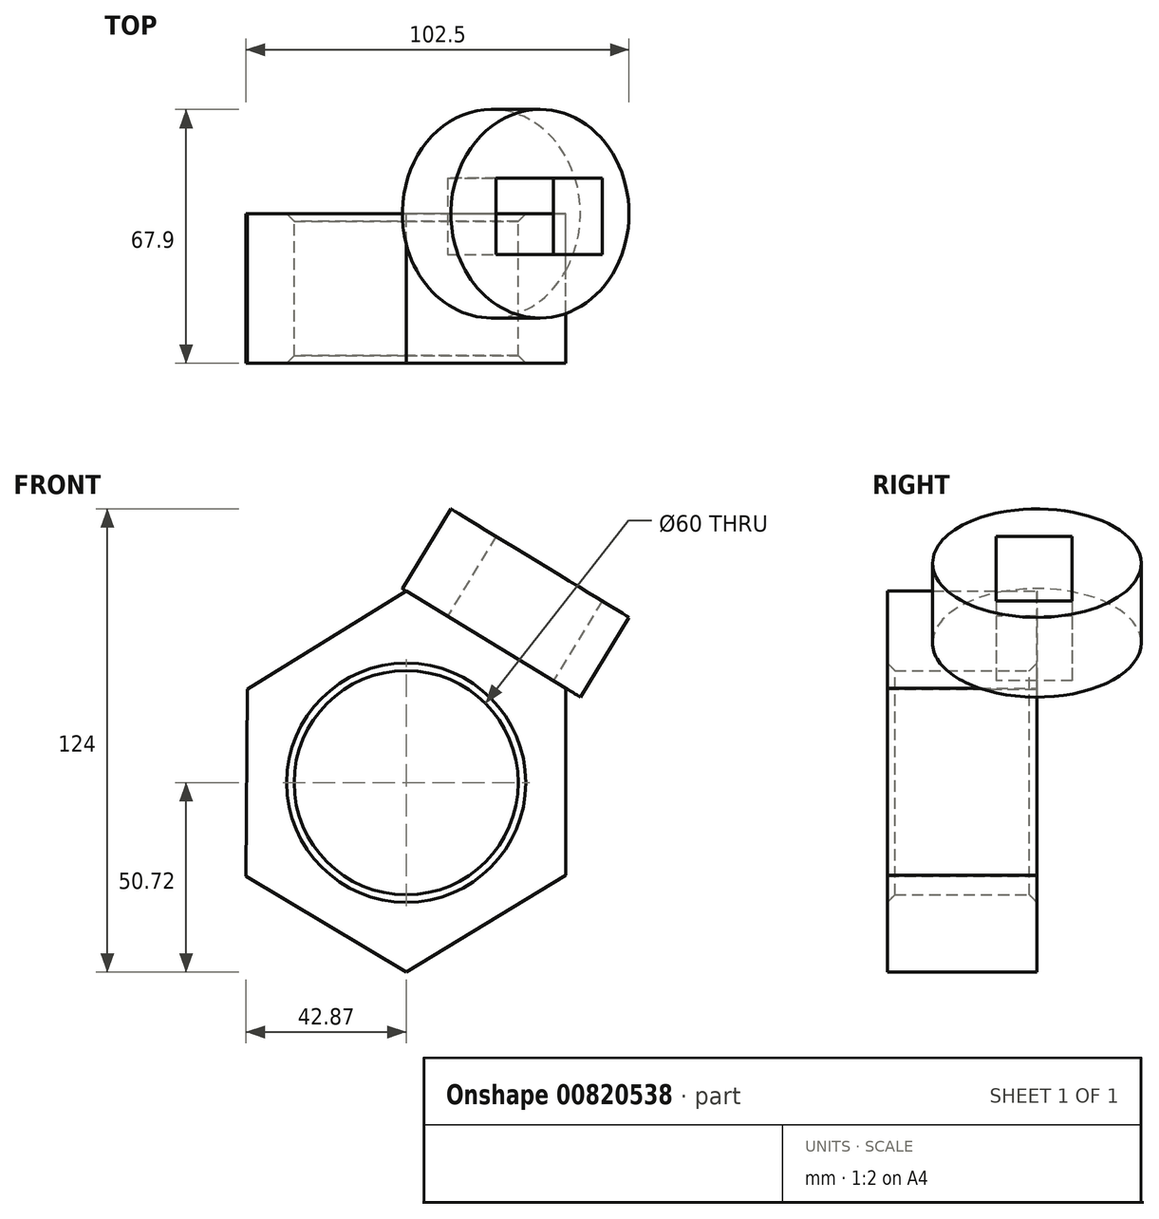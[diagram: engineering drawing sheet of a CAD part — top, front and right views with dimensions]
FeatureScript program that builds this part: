
annotation { "Feature Type Name" : "Feature", "Feature Type Description" : "" }
export const myFeature = defineFeature(function(context is Context, id is Id, definition is map)
    precondition{}
    {
        {
            var Q0;
            Q0=qCreatedBy(makeId("Front.planeOp"),FACE);
            var sketch = newSketch(context, id + "F0", { "sketchPlane" : qUnion([Q0])});
            skCircle(sketch, "E0", {"center": v(0, 0) * mm, "radius": 30 * mm});
            skLineSegment(sketch, "E1", {"start": v(-42.52, 25) * mm, "end": v(0, 51.3) * mm});
            skLineSegment(sketch, "E2", {"start": v(0, 51.3) * mm, "end": v(42.7, 25.29) * mm});
            skLineSegment(sketch, "E3", {"start": v(42.7, 25.29) * mm, "end": v(42.7, -24.71) * mm});
            skLineSegment(sketch, "E4", {"start": v(42.7, -24.71) * mm, "end": v(0, -50.72) * mm});
            skLineSegment(sketch, "E5", {"start": v(0, -50.72) * mm, "end": v(-42.87, -25) * mm});
            skLineSegment(sketch, "E6", {"start": v(-42.52, 25) * mm, "end": v(-42.87, -25) * mm});
            skSolve(sketch);
        }
        {
            var Q0;
            Q0=makeQuery(id+"F0.imprint","IMPRINT",FACE,{"disambiguationData":[TD([[makeQuery(id+"F0.imprint","IMPRINT",EDGE,{"derivedFrom":sQuery(id+"F0.wireOp",EDGE,"E0")}),-1.0]])]});
            extrude(context, id + "F1", {"entities" : qUnion([Q0]), "depth" : 40 * mm, "offsetDistance" : 25 * mm});
        }
        {
            var Q0;
            Q0=makeQuery(id+"F1.opExtrude","CAP_EDGE",EDGE,{"disambiguationData":[OSD([sQuery(id+"F0.wireOp",EDGE,"E0")])],"isStart":false});
            var Q1;
            Q1=makeQuery(id+"F1.opExtrude","CAP_EDGE",EDGE,{"disambiguationData":[OSD([sQuery(id+"F0.wireOp",EDGE,"E0")])],"isStart":true});
            chamfer(context, id + "F2", {"entities" : qUnion([Q0, Q1]), "width" : 2 * mm, "tangentPropagation" : true});
        }
        {
            var Q0;
            Q0=makeQuery(id+"F1.opExtrude","SWEPT_FACE",FACE,{"disambiguationData":[OSD([sQuery(id+"F0.wireOp",EDGE,"E2")])]});
            var sketch = newSketch(context, id + "F3", { "sketchPlane" : qUnion([Q0])});
            skCircle(sketch, "E7", {"center": v(0, 0) * mm, "radius": 27.9 * mm});
            skLineSegment(sketch, "E8.bottom", {"start": v(-13.76, 9.48) * mm, "end": v(19.48, 9.48) * mm});
            skLineSegment(sketch, "E8.top", {"start": v(-13.76, -10.9) * mm, "end": v(19.48, -10.9) * mm});
            skLineSegment(sketch, "E8.left", {"start": v(-13.76, 9.48) * mm, "end": v(-13.76, -10.9) * mm});
            skLineSegment(sketch, "E8.right", {"start": v(19.48, 9.48) * mm, "end": v(19.48, -10.9) * mm});
            skSolve(sketch);
        }
        {
            var Q0;
            Q0 = qSketchRegion(id + "F3", true);
            extrude(context, id + "F4", {"entities" : qUnion([Q0]), "operationType" : NewBodyOperationType.ADD, "depth" : 25 * mm, "offsetDistance" : 25 * mm});
        }
    });
